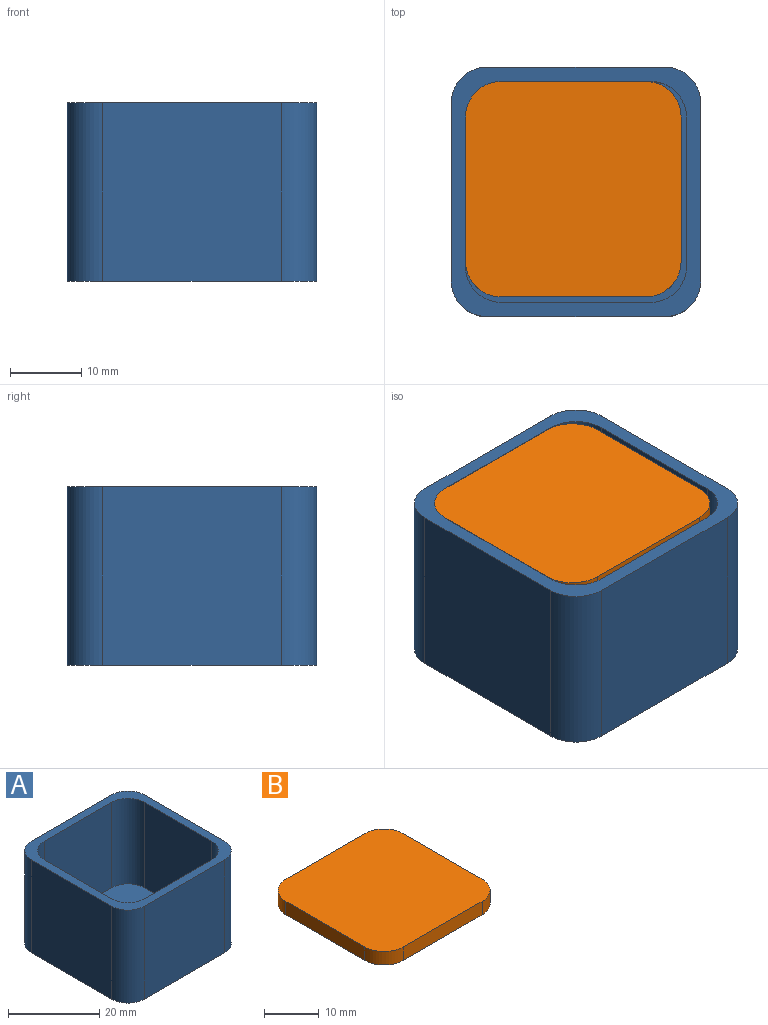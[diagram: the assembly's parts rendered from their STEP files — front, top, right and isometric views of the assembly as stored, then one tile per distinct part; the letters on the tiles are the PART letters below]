
ASSEMBLY  parts=2 mates=1
PART A: 19 faces, bbox 35x35x25 mm
  f0: plane 35x35mm, normal (0,0,1), area 264mm2, adj f1,f2,f3,f4,f6,f7,f8,f9
  f1: plane 25x25mm, normal (-1,0,0), area 625mm2, adj f0,f5,f15,f18
  f2: plane 25x25mm, normal (0,-1,0), area 625mm2, adj f0,f5,f15,f16
  f3: plane 25x25mm, normal (1,0,0), area 625mm2, adj f0,f5,f16,f17
  f4: plane 25x25mm, normal (0,1,0), area 625mm2, adj f0,f5,f17,f18
  f5: plane 35x35mm, normal (0,0,-1), area 1203.5mm2, adj f1,f2,f3,f4,f15,f16,f17,f18
  f6: plane 23x21mm, normal (1,0,0), area 483mm2, adj f0,f10,f12,f14
  f7: plane 23x21mm, normal (0,1,0), area 483mm2, adj f0,f10,f13,f14
  f8: plane 23x21mm, normal (-1,0,0), area 483mm2, adj f0,f10,f11,f13
  f9: plane 23x21mm, normal (0,-1,0), area 483mm2, adj f0,f10,f11,f12
  f10: plane 31x31mm, normal (0,0,1), area 939.5mm2, adj f6,f7,f8,f9,f11,f12,f13,f14
  f11: cylinder r=5mm len=23mm, axis (0,0,-1), area 180.6mm2, adj f0,f8,f9,f10
  f12: cylinder r=5mm len=23mm, axis (0,0,1), area 180.6mm2, adj f0,f6,f9,f10
  f13: cylinder r=5mm len=23mm, axis (0,0,1), area 180.6mm2, adj f0,f7,f8,f10
  f14: cylinder r=5mm len=23mm, axis (0,0,-1), area 180.6mm2, adj f0,f6,f7,f10
  f15: cylinder r=5mm len=25mm, axis (0,0,1), area 196.3mm2, adj f0,f1,f2,f5
  f16: cylinder r=5mm len=25mm, axis (0,0,-1), area 196.3mm2, adj f0,f2,f3,f5
  f17: cylinder r=5mm len=25mm, axis (0,0,1), area 196.3mm2, adj f0,f3,f4,f5
  f18: cylinder r=5mm len=25mm, axis (0,0,-1), area 196.3mm2, adj f0,f1,f4,f5
PART B: 10 faces, bbox 30.3x30.3x3 mm
  f0: plane 20.25x3mm, normal (-1,0,0), area 60.8mm2, adj f4,f5,f6,f9
  f1: plane 20.25x3mm, normal (0,-1,0), area 60.8mm2, adj f4,f5,f6,f7
  f2: plane 20.25x3mm, normal (1,0,0), area 60.8mm2, adj f4,f5,f7,f8
  f3: plane 20.25x3mm, normal (0,1,0), area 60.8mm2, adj f4,f5,f8,f9
  f4: plane 30.25x30.25mm, normal (0,0,1), area 893.6mm2, adj f0,f1,f2,f3,f6,f7,f8,f9
  f5: plane 30.25x30.25mm, normal (0,0,-1), area 893.6mm2, adj f0,f1,f2,f3,f6,f7,f8,f9
  f6: cylinder r=5mm len=5mm, axis (0,0,1), area 23.6mm2, adj f0,f1,f4,f5
  f7: cylinder r=5mm len=5mm, axis (0,0,-1), area 23.6mm2, adj f1,f2,f4,f5
  f8: cylinder r=5mm len=5mm, axis (0,0,1), area 23.6mm2, adj f2,f3,f4,f5
  f9: cylinder r=5mm len=5mm, axis (0,0,-1), area 23.6mm2, adj f0,f3,f4,f5
PLACE A t=(-10.17,-12.18,-27.6)mm
PLACE B t=(-8.17,-9.43,-5.6)mm fixed
MATE fastened B.f4 <-> A.f0  axis (0,0,1) through (-3.17,20.82,-2.6)mm
